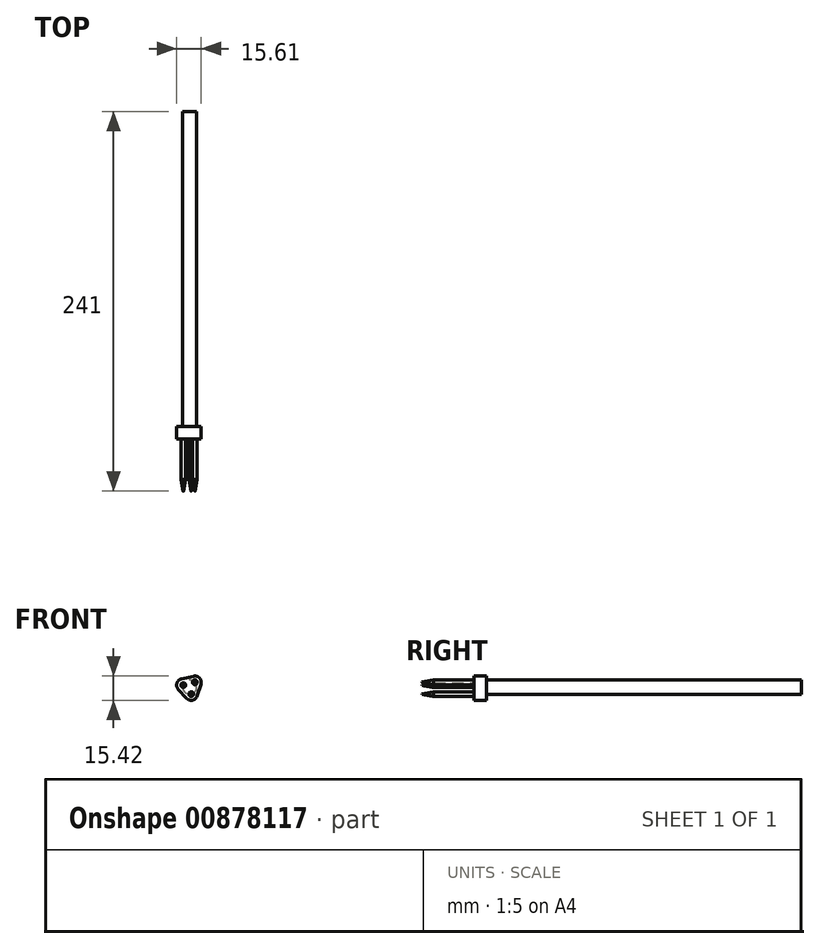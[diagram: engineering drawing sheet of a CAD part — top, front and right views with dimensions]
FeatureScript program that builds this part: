
annotation { "Feature Type Name" : "Feature", "Feature Type Description" : "" }
export const myFeature = defineFeature(function(context is Context, id is Id, definition is map)
    precondition{}
    {
        {
            var Q0;
            Q0=qCreatedBy(makeId("Front.planeOp"),FACE);
            var sketch = newSketch(context, id + "F0", { "sketchPlane" : qUnion([Q0])});
            skCircle(sketch, "E0", {"center": v(0, 0) * mm, "radius": 4.5 * mm});
            skSolve(sketch);
        }
        {
            var Q0;
            Q0=makeQuery(id+"F0.imprint","IMPRINT",FACE,{"disambiguationData":[TD([[makeQuery(id+"F0.imprint","IMPRINT",EDGE,{"derivedFrom":sQuery(id+"F0.wireOp",EDGE,"E0")}),1.0]])]});
            extrude(context, id + "F1", {"entities" : qUnion([Q0]), "depth" : 200 * mm, "offsetDistance" : 25 * mm});
        }
        {
            var Q0;
            Q0=makeQuery(id+"F1.opExtrude","CAP_FACE",FACE,{"disambiguationData":[OSD([sQuery(id+"F0.wireOp",EDGE,"E0")])],"isStart":false});
            var sketch = newSketch(context, id + "F2", { "sketchPlane" : qUnion([Q0])});
            skCircle(sketch, "E1.cCircle", {"center": v(0, 0) * mm, "radius": 12.5 * mm, "construction": true});
            skLineSegment(sketch, "E1.0", {"start": v(-5.15, 5.27) * mm, "end": v(2.46, 6.94) * mm});
            skLineSegment(sketch, "E1.1", {"start": v(7.14, 1.83) * mm, "end": v(4.78, -5.6) * mm});
            skLineSegment(sketch, "E1.2", {"start": v(-1.99, -7.1) * mm, "end": v(-7.24, -1.34) * mm});
            skPoint(sketch, "E2.visualSharp", {"position": v(9.23, 8.43) * mm});
            skArc(sketch, "E2.filletArc", {"start": v(7.14, 1.83) * mm, "mid": v(6.28, 5.73) * mm, "end": v(2.46, 6.94) * mm});
            skPoint(sketch, "E3.visualSharp", {"position": v(-11.92, 3.78) * mm});
            skArc(sketch, "E3.filletArc", {"start": v(-5.15, 5.27) * mm, "mid": v(-8.1, 2.57) * mm, "end": v(-7.24, -1.34) * mm});
            skPoint(sketch, "E4.visualSharp", {"position": v(2.69, -12.2) * mm});
            skArc(sketch, "E4.filletArc", {"start": v(-1.99, -7.1) * mm, "mid": v(1.83, -8.3) * mm, "end": v(4.78, -5.6) * mm});
            skSolve(sketch);
        }
        {
            var Q0;
            Q0=makeQuery(id+"F2.imprint","IMPRINT",FACE,{"disambiguationData":[TD([[makeQuery(id+"F2.imprint","IMPRINT",EDGE,{"derivedFrom":sQuery(id+"F2.wireOp",EDGE,"E1.0")}),-1.0]])]});
            var Q1;
            Q1=makeQuery(id+"F2.imprint","IMPRINT",FACE,{"disambiguationData":[TD([[makeQuery(id+"F2.imprint","IMPRINT",EDGE,{"derivedFrom":makeQuery(id+"F1.opExtrude","CAP_EDGE",EDGE,{"disambiguationData":[OSD([sQuery(id+"F0.wireOp",EDGE,"E0")])],"isStart":false})}),1.0]])]});
            extrude(context, id + "F3", {"entities" : qUnion([Q0, Q1]), "operationType" : NewBodyOperationType.ADD, "depth" : 8 * mm, "offsetDistance" : 25 * mm});
        }
        {
            var Q0;
            Q0=makeQuery(id+"F3.opExtrude","CAP_FACE",FACE,{"disambiguationData":[OSD([sQuery(id+"F2.wireOp",EDGE,"E1.0"),sQuery(id+"F2.wireOp",EDGE,"E1.1"),sQuery(id+"F2.wireOp",EDGE,"E1.2"),sQuery(id+"F2.wireOp",EDGE,"E2.filletArc"),sQuery(id+"F2.wireOp",EDGE,"E3.filletArc"),sQuery(id+"F2.wireOp",EDGE,"E4.filletArc")])],"isStart":false});
            var sketch = newSketch(context, id + "F4", { "sketchPlane" : qUnion([Q0])});
            skLineSegment(sketch, "E5", {"start": v(-4.61, -4.22) * mm, "end": v(6.28, 5.73) * mm, "construction": true});
            skLineSegment(sketch, "E6", {"start": v(5.96, -1.89) * mm, "end": v(-8.1, 2.57) * mm, "construction": true});
            skLineSegment(sketch, "E7", {"start": v(-1.34, 6.1) * mm, "end": v(1.83, -8.3) * mm, "construction": true});
            skLineSegment(sketch, "E8", {"start": v(6.28, 5.73) * mm, "end": v(2.36, 2.15) * mm, "construction": true});
            skLineSegment(sketch, "E9", {"start": v(-8.1, 2.57) * mm, "end": v(0, 0) * mm, "construction": true});
            skCircle(sketch, "E10", {"center": v(-4.05, 1.28) * mm, "radius": 1.5 * mm});
            skLineSegment(sketch, "E11", {"start": v(0, 0) * mm, "end": v(6.28, 5.73) * mm, "construction": true});
            skLineSegment(sketch, "E12", {"start": v(0, 0) * mm, "end": v(1.83, -8.3) * mm, "construction": true});
            skCircle(sketch, "E13", {"center": v(3.32, 3.03) * mm, "radius": 1.5 * mm});
            skCircle(sketch, "E14", {"center": v(0.97, -4.4) * mm, "radius": 1.5 * mm});
            skSolve(sketch);
        }
        {
            var Q0;
            Q0=makeQuery(id+"F4.imprint","IMPRINT",FACE,{"disambiguationData":[TD([[makeQuery(id+"F4.imprint","IMPRINT",EDGE,{"derivedFrom":sQuery(id+"F4.wireOp",EDGE,"E13")}),1.0]])]});
            var Q1;
            Q1=makeQuery(id+"F4.imprint","IMPRINT",FACE,{"disambiguationData":[TD([[makeQuery(id+"F4.imprint","IMPRINT",EDGE,{"derivedFrom":sQuery(id+"F4.wireOp",EDGE,"E10")}),1.0]])]});
            var Q2;
            Q2=makeQuery(id+"F4.imprint","IMPRINT",FACE,{"disambiguationData":[TD([[makeQuery(id+"F4.imprint","IMPRINT",EDGE,{"derivedFrom":sQuery(id+"F4.wireOp",EDGE,"E14")}),1.0]])]});
            extrude(context, id + "F5", {"entities" : qUnion([Q0, Q1, Q2]), "operationType" : NewBodyOperationType.ADD, "depth" : 33 * mm, "offsetDistance" : 25 * mm});
        }
        {
            var Q0;
            Q0=makeQuery(id+"F5.opExtrude","CAP_FACE",FACE,{"disambiguationData":[OSD([sQuery(id+"F4.wireOp",EDGE,"E10")])],"isStart":false});
            var Q1;
            Q1=makeQuery(id+"F5.opExtrude","CAP_FACE",FACE,{"disambiguationData":[OSD([sQuery(id+"F4.wireOp",EDGE,"E13")])],"isStart":false});
            var Q2;
            Q2=makeQuery(id+"F5.opExtrude","CAP_FACE",FACE,{"disambiguationData":[OSD([sQuery(id+"F4.wireOp",EDGE,"E14")])],"isStart":false});
            chamfer(context, id + "F6", {"entities" : qUnion([Q0, Q1, Q2]), "chamferType" : ChamferType.OFFSET_ANGLE, "width" : 1.3 * mm, "oppositeDirection" : false, "angle" : 80 * degree, "tangentPropagation" : true});
        }
    });
